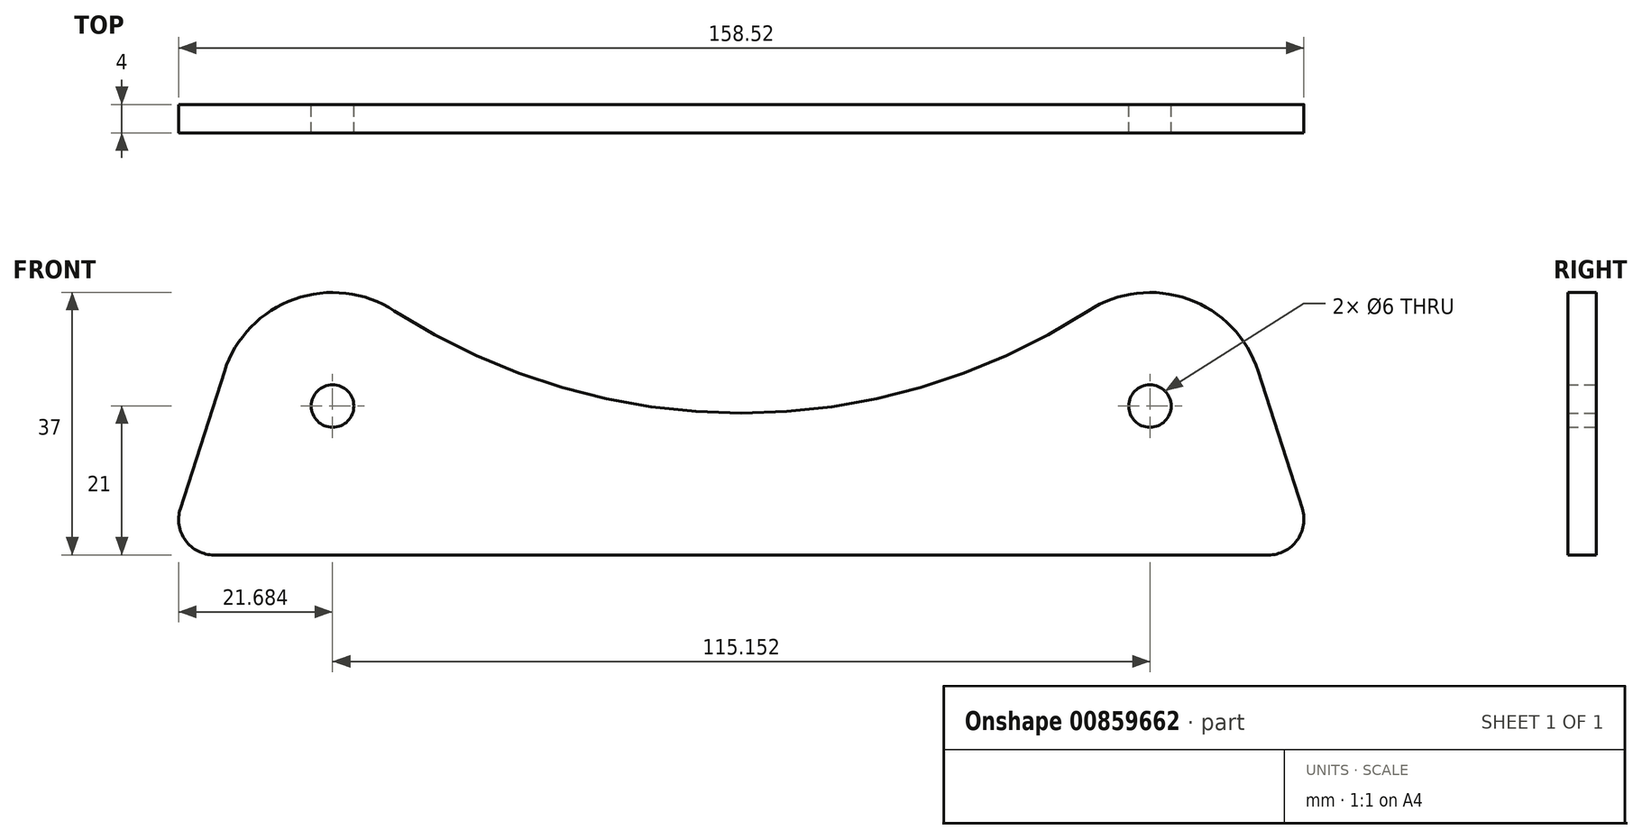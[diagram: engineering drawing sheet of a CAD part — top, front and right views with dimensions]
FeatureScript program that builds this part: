
annotation { "Feature Type Name" : "Feature", "Feature Type Description" : "" }
export const myFeature = defineFeature(function(context is Context, id is Id, definition is map)
    precondition{}
    {
        {
            var Q0;
            Q0=qCreatedBy(makeId("Front.planeOp"),FACE);
            var sketch = newSketch(context, id + "F0", { "sketchPlane" : qUnion([Q0])});
            skCircle(sketch, "E0", {"center": v(0, 0) * mm, "radius": 100 * mm, "construction": true});
            skCircle(sketch, "E1", {"center": v(-57.58, -89) * mm, "radius": 6 * mm, "construction": true});
            skCircle(sketch, "E2", {"center": v(57.58, -89) * mm, "radius": 6 * mm, "construction": true});
            skCircle(sketch, "E3", {"center": v(-57.58, -89) * mm, "radius": 3 * mm});
            skCircle(sketch, "E4", {"center": v(57.58, -89) * mm, "radius": 3 * mm});
            skArc(sketch, "E5.0", {"start": v(-48.89, -75.57) * mm, "mid": v(0, -90) * mm, "end": v(48.89, -75.57) * mm});
            skArc(sketch, "E6.0", {"start": v(-48.89, -75.57) * mm, "mid": v(-62.96, -73.93) * mm, "end": v(-72.81, -84.12) * mm});
            skArc(sketch, "E7", {"start": v(72.81, -84.12) * mm, "mid": v(62.96, -73.93) * mm, "end": v(48.89, -75.57) * mm});
            skLineSegment(sketch, "E8", {"start": v(-72.81, -84.12) * mm, "end": v(-79.02, -103.47) * mm});
            skLineSegment(sketch, "E9", {"start": v(-74.26, -110) * mm, "end": v(32.7, -110) * mm});
            skLineSegment(sketch, "E10", {"start": v(32.7, -110) * mm, "end": v(61.96, -110) * mm});
            skLineSegment(sketch, "E11", {"start": v(61.96, -110) * mm, "end": v(74.26, -110) * mm});
            skLineSegment(sketch, "E12", {"start": v(79.02, -103.47) * mm, "end": v(72.81, -84.12) * mm});
            skLineSegment(sketch, "E13", {"start": v(0, 0) * mm, "end": v(0, -157.3) * mm, "construction": true});
            skPoint(sketch, "E14.visualSharp", {"position": v(-81.11, -110) * mm});
            skArc(sketch, "E14.filletArc", {"start": v(-79.02, -103.47) * mm, "mid": v(-78.3, -107.95) * mm, "end": v(-74.26, -110) * mm});
            skPoint(sketch, "E15.visualSharp", {"position": v(81.11, -110) * mm});
            skArc(sketch, "E15.filletArc", {"start": v(74.26, -110) * mm, "mid": v(78.3, -107.95) * mm, "end": v(79.02, -103.47) * mm});
            skSolve(sketch);
        }
        {
            var Q0;
            Q0=makeQuery(id+"F0.imprint","IMPRINT",FACE,{"disambiguationData":[TD([[makeQuery(id+"F0.imprint","IMPRINT",EDGE,{"derivedFrom":sQuery(id+"F0.wireOp",EDGE,"E3")}),-1.0]])]});
            extrude(context, id + "F1", {"entities" : qUnion([Q0]), "depth" : 4 * mm, "offsetDistance" : 25 * mm});
        }
    });
